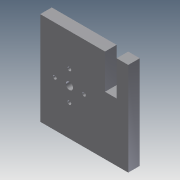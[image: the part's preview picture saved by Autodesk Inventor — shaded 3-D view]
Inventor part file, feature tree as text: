
AUTODESK INVENTOR PART (.ipt)
format: ipt  version: 2011 (Build 150239000, 239)  size: 130,560 bytes
history: native  units: in
note: dims shown in document units (in); Inventor stores cm internally (conversion verified against a paired STEP export)
features: extrude x6, sketch x6
ambient origin geometry x8: Origin, YZ Plane, XZ Plane, XY Plane, X Axis, Y Axis, Z Axis, Center Point
bodies: Solid1 (feature_tree)
feature tree (12):
  extrude  "Extrusion1"  Depth=2.0079in
  extrude  "Extrusion2"  Depth=0.9843in
  extrude  "Extrusion3"  Depth=0.0787in
  extrude  "Extrusion4"  Depth=0.0787in
  extrude  "Extrusion5"  Depth=0.6299in
  extrude  "Extrusion6"  Depth=0.156in
  sketch  "Sketch1"  dims[d0=1.7717in d1=2.0079in]
  sketch  "Sketch2"  dims[d2=0.125in d3=0.0in d4=0.9843in]
  sketch  "Sketch3"  dims[d6=0.6299in d7=0.0787in]
  sketch  "Sketch4"  dims[d8=0.0787in d9=0.0787in]
  sketch  "Sketch5"  dims[d10=0.0787in d11=0.6299in]
  sketch  "Sketch6"  dims[d12=1.0in d13=0.0in d14=0.156in d15=1.0in d16=0.0in d17=0.25in d18=0.125in d19=0.0in d20=0.125in d21=0.0in d22=0.25in d23=0.25in d24=0.5in d25=0.25in d26=1.0in d27=0.0in]
